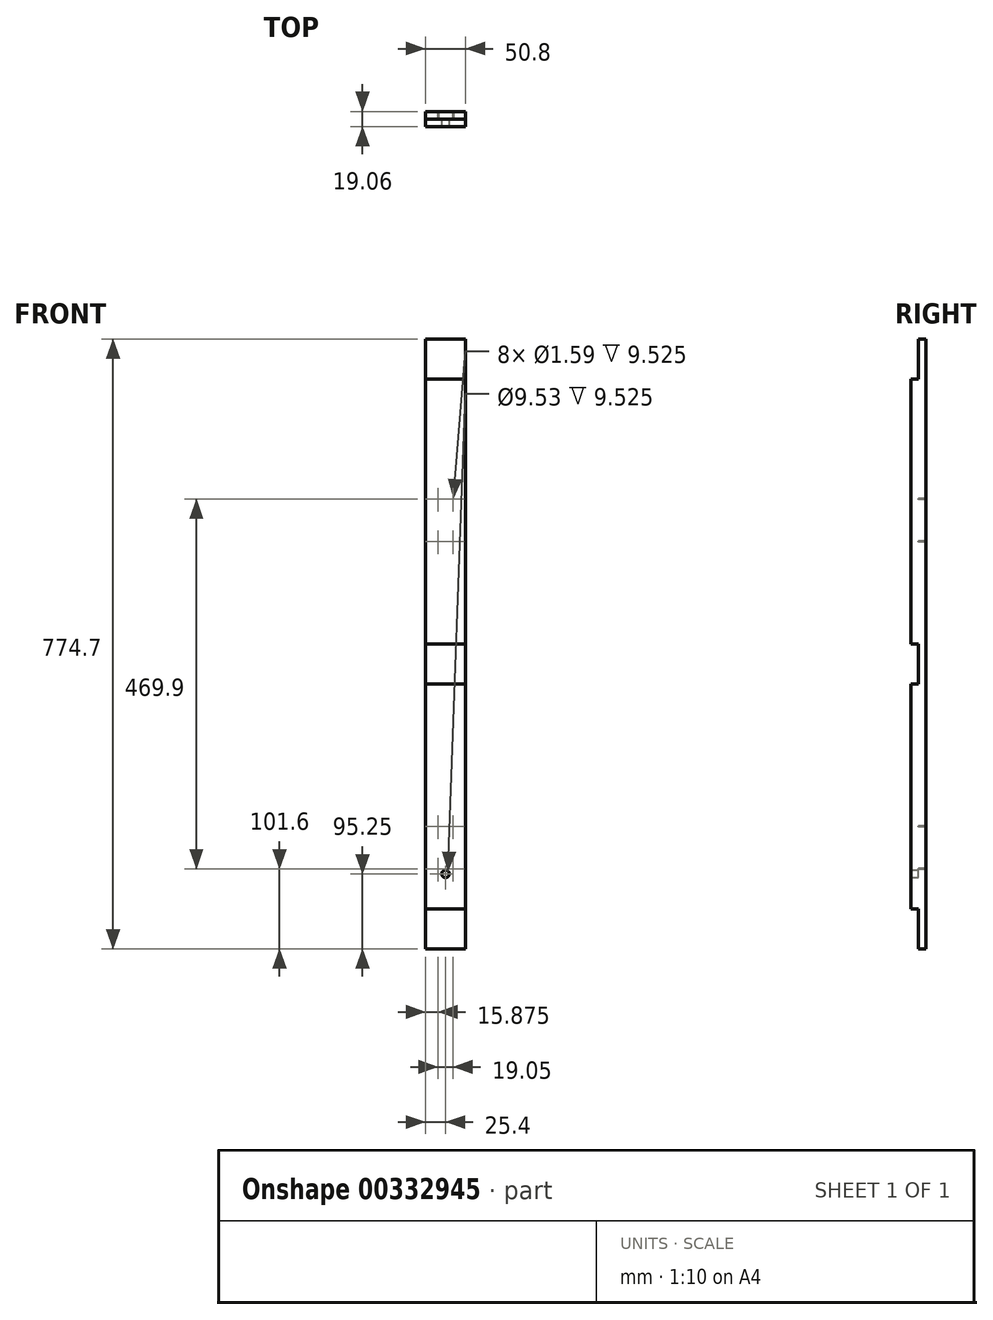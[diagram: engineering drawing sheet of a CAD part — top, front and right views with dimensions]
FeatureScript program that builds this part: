
annotation { "Feature Type Name" : "Feature", "Feature Type Description" : "" }
export const myFeature = defineFeature(function(context is Context, id is Id, definition is map)
    precondition{}
    {
        {
            var Q0;
            Q0=qCreatedBy(makeId("Top.planeOp"),FACE);
            var sketch = newSketch(context, id + "F0", { "sketchPlane" : qUnion([Q0])});
            skLineSegment(sketch, "E0.bottom", {"start": v(25.4, 9.53) * mm, "end": v(-25.4, 9.53) * mm});
            skLineSegment(sketch, "E0.top", {"start": v(25.4, -9.53) * mm, "end": v(-25.4, -9.53) * mm});
            skLineSegment(sketch, "E0.left", {"start": v(25.4, 9.53) * mm, "end": v(25.4, -9.52) * mm});
            skLineSegment(sketch, "E0.right", {"start": v(-25.4, 9.53) * mm, "end": v(-25.4, -9.53) * mm});
            skPoint(sketch, "E0.middle", {"position": v(0, 0) * mm});
            skSolve(sketch);
        }
        {
            var Q0;
            Q0=makeQuery(id+"F0.imprint","IMPRINT",FACE,{"disambiguationData":[TD([[makeQuery(id+"F0.imprint","IMPRINT",EDGE,{"derivedFrom":sQuery(id+"F0.wireOp",EDGE,"E0.bottom")}),1.0]])]});
            var Q1;
            Q1=qSketchRegion(id+"F2",true);
            extrude(context, id + "F1", {"entities" : qUnion([Q0, Q1]), "depth" : 774.7 * mm});
        }
        {
            var Q0;
            Q0=qCreatedBy(makeId("Front.planeOp"),FACE);
            var sketch = newSketch(context, id + "F2", { "sketchPlane" : qUnion([Q0])});
            skLineSegment(sketch, "E1.bottom", {"start": v(-38.77, 0) * mm, "end": v(83.66, 0) * mm});
            skLineSegment(sketch, "E1.top", {"start": v(-38.77, 50.8) * mm, "end": v(83.66, 50.8) * mm});
            skLineSegment(sketch, "E1.left", {"start": v(-38.77, 0) * mm, "end": v(-38.77, 50.8) * mm});
            skLineSegment(sketch, "E1.right", {"start": v(83.66, 0) * mm, "end": v(83.66, 50.8) * mm});
            skLineSegment(sketch, "E2.bottom", {"start": v(-210.36, 723.9) * mm, "end": v(132.8, 723.9) * mm});
            skLineSegment(sketch, "E2.top", {"start": v(-210.36, 774.7) * mm, "end": v(132.8, 774.7) * mm});
            skLineSegment(sketch, "E2.left", {"start": v(-210.36, 723.9) * mm, "end": v(-210.36, 774.7) * mm});
            skLineSegment(sketch, "E2.right", {"start": v(132.8, 723.9) * mm, "end": v(132.8, 774.7) * mm});
            skLineSegment(sketch, "E3.bottom", {"start": v(-194.26, 387.35) * mm, "end": v(102.12, 387.35) * mm});
            skLineSegment(sketch, "E3.top", {"start": v(-194.26, 336.55) * mm, "end": v(102.12, 336.55) * mm});
            skLineSegment(sketch, "E3.left", {"start": v(-194.26, 387.35) * mm, "end": v(-194.26, 336.55) * mm});
            skLineSegment(sketch, "E3.right", {"start": v(102.12, 387.35) * mm, "end": v(102.12, 336.55) * mm});
            skSolve(sketch);
        }
        {
            var Q0;
            Q0=qSketchRegion(id+"F2",true);
            extrude(context, id + "F3", {"entities" : qUnion([Q0]), "operationType" : NewBodyOperationType.REMOVE, "depth" : 25.4 * mm});
        }
        {
            var Q0;
            Q0=qCreatedBy(makeId("Front.planeOp"),FACE);
            var sketch = newSketch(context, id + "F4", { "sketchPlane" : qUnion([Q0])});
            skCircle(sketch, "E4", {"center": v(9.53, 101.6) * mm, "radius": 0.8 * mm});
            skCircle(sketch, "E5", {"center": v(9.52, 155.58) * mm, "radius": 0.8 * mm});
            skCircle(sketch, "E6", {"center": v(9.52, 517.52) * mm, "radius": 0.8 * mm});
            skCircle(sketch, "E7", {"center": v(9.52, 571.5) * mm, "radius": 0.8 * mm});
            skLineSegment(sketch, "E8", {"start": v(0, 0) * mm, "end": v(0, 1192.46) * mm, "construction": true});
            skLineSegment(sketch, "E9.bottom", {"start": v(9.52, 101.6) * mm, "end": v(-9.52, 101.6) * mm, "construction": true});
            skLineSegment(sketch, "E9.left", {"start": v(9.53, 101.6) * mm, "end": v(9.52, 571.5) * mm, "construction": true});
            skLineSegment(sketch, "E9.right", {"start": v(-9.53, 101.6) * mm, "end": v(-9.53, 571.5) * mm, "construction": true});
            skCircle(sketch, "E10", {"center": v(-9.53, 517.52) * mm, "radius": 0.8 * mm});
            skCircle(sketch, "E11", {"center": v(-9.53, 571.5) * mm, "radius": 0.8 * mm});
            skCircle(sketch, "E12", {"center": v(-9.53, 101.6) * mm, "radius": 0.8 * mm});
            skCircle(sketch, "E13", {"center": v(-9.53, 155.58) * mm, "radius": 0.8 * mm});
            skSolve(sketch);
        }
        {
            var Q0;
            Q0=qSketchRegion(id+"F4",true);
            extrude(context, id + "F5", {"entities" : qUnion([Q0]), "operationType" : NewBodyOperationType.REMOVE, "oppositeDirection" : true, "depth" : 25.4 * mm});
        }
        {
            var Q0;
            Q0=qCreatedBy(makeId("Front.planeOp"),FACE);
            var sketch = newSketch(context, id + "F6", { "sketchPlane" : qUnion([Q0])});
            skCircle(sketch, "E14", {"center": v(0, 95.25) * mm, "radius": 4.76 * mm});
            skCircle(sketch, "E15", {"center": v(0, 361.95) * mm, "radius": 4.76 * mm});
            skSolve(sketch);
        }
        {
            var Q0;
            Q0=qSketchRegion(id+"F6",true);
            extrude(context, id + "F7", {"entities" : qUnion([Q0]), "operationType" : NewBodyOperationType.REMOVE, "depth" : 25.4 * mm});
        }
    });
